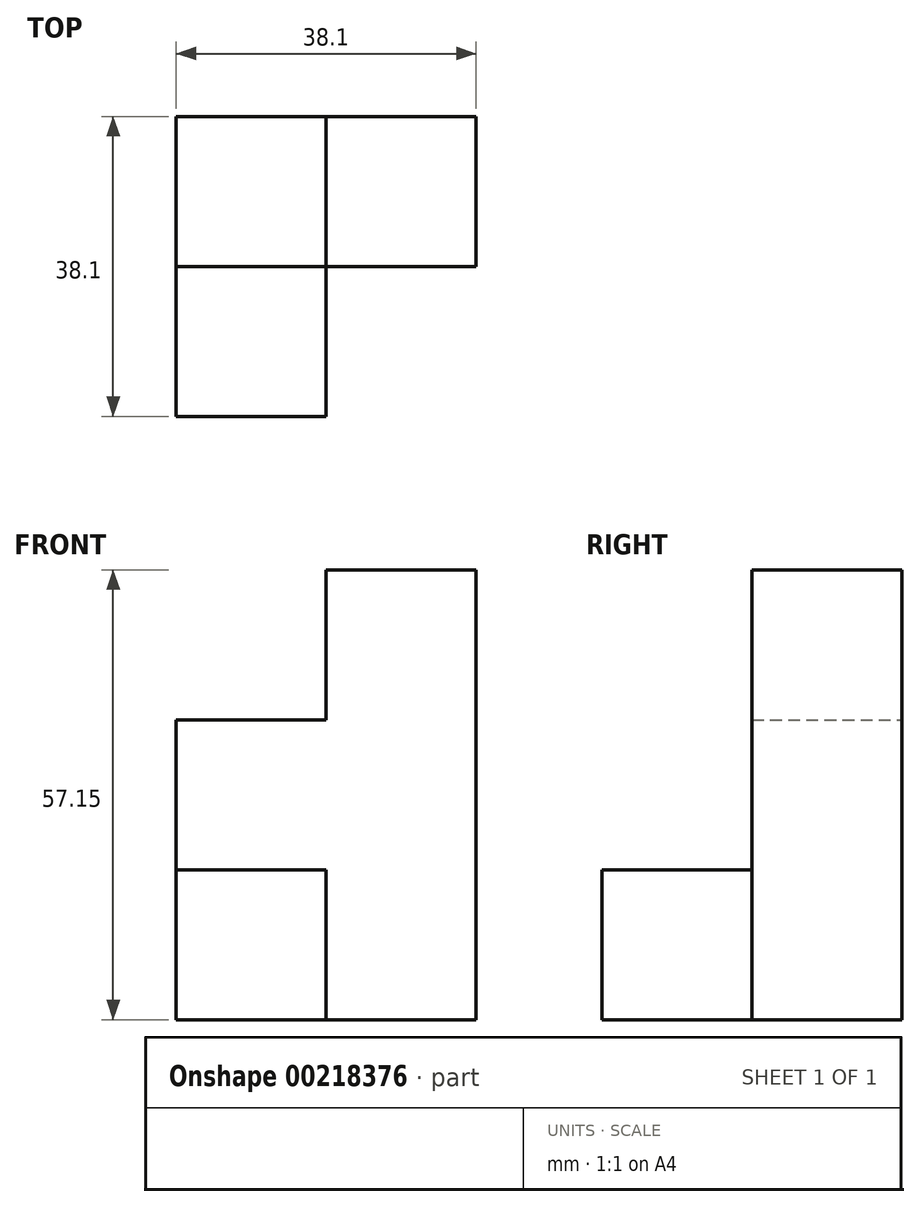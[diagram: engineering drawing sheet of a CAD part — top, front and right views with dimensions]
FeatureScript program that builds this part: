
annotation { "Feature Type Name" : "Feature", "Feature Type Description" : "" }
export const myFeature = defineFeature(function(context is Context, id is Id, definition is map)
    precondition{}
    {
        {
            var Q0;
            Q0=qCreatedBy(makeId("Front.planeOp"),FACE);
            var sketch = newSketch(context, id + "F0", { "sketchPlane" : qUnion([Q0])});
            skLineSegment(sketch, "E0.bottom", {"start": v(-22.03, -20.07) * mm, "end": v(-41.08, -20.07) * mm});
            skLineSegment(sketch, "E0.top", {"start": v(-22.03, -1.02) * mm, "end": v(-41.08, -1.02) * mm});
            skLineSegment(sketch, "E0.left", {"start": v(-22.03, -20.07) * mm, "end": v(-22.03, -1.02) * mm});
            skLineSegment(sketch, "E0.right", {"start": v(-41.08, -20.07) * mm, "end": v(-41.08, -1.02) * mm});
            skPoint(sketch, "E0.middle", {"position": v(-31.55, -10.54) * mm});
            skLineSegment(sketch, "E1", {"start": v(-22.03, -20.07) * mm, "end": v(-2.98, -20.07) * mm});
            skLineSegment(sketch, "E2", {"start": v(-2.98, 18.03) * mm, "end": v(-2.98, -20.07) * mm});
            skLineSegment(sketch, "E3", {"start": v(-2.98, 18.03) * mm, "end": v(-41.08, 18.03) * mm});
            skLineSegment(sketch, "E4", {"start": v(-41.08, 18.03) * mm, "end": v(-41.08, -1.02) * mm});
            skLineSegment(sketch, "E5", {"start": v(-2.98, 18.03) * mm, "end": v(-2.98, 37.08) * mm});
            skLineSegment(sketch, "E6", {"start": v(-2.98, 37.08) * mm, "end": v(-22.03, 37.08) * mm});
            skLineSegment(sketch, "E7", {"start": v(-22.03, 37.08) * mm, "end": v(-22.03, 18.03) * mm});
            skSolve(sketch);
        }
        {
            var Q0;
            {var subQ0=sQuery(id+"F0.wireOp",EDGE,"E5");Q0=makeQuery(id+"F0.imprint","IMPRINT",FACE,{"disambiguationData":[TD([[makeQuery(id+"F0.imprint","IMPRINT",EDGE,{"derivedFrom":subQ0}),1.0]])]});}
            extrude(context, id + "F1", {"entities" : qUnion([Q0]), "depth" : 19.05 * mm});
        }
        {
            var Q0;
            Q0=makeQuery(id+"F0.imprint","IMPRINT",FACE,{"disambiguationData":[TD([[makeQuery(id+"F0.imprint","IMPRINT",EDGE,{"derivedFrom":sQuery(id+"F0.wireOp",EDGE,"E0.top")}),-1.0]])]});
            extrude(context, id + "F2", {"entities" : qUnion([Q0]), "operationType" : NewBodyOperationType.ADD, "depth" : 19.05 * mm});
        }
        {
            var Q0;
            Q0=makeQuery(id+"F0.imprint","IMPRINT",FACE,{"disambiguationData":[TD([[makeQuery(id+"F0.imprint","IMPRINT",EDGE,{"derivedFrom":sQuery(id+"F0.wireOp",EDGE,"E0.bottom")}),-1.0]])]});
            extrude(context, id + "F3", {"entities" : qUnion([Q0]), "operationType" : NewBodyOperationType.ADD, "depth" : 38.1 * mm});
        }
    });
